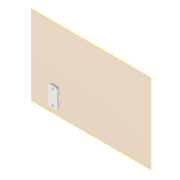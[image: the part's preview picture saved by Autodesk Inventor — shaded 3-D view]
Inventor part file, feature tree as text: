
AUTODESK INVENTOR PART (.ipt)
format: ipt  version: 2022 (Build 260153000, 153)  size: 105,472 bytes
history: native  units: mm
features: reference x6, other x4, extrude x2, sketch x2, plane x1, fillet x1
ambient origin geometry x8: Origin, YZ Plane, XZ Plane, XY Plane, X Axis, Y Axis, Z Axis, Center Point
bodies: Volumenkörper1 (feature_tree)
feature tree (16):
  plane  "Arbeitsebene1"
  extrude  "Extrusion1"  Depth=3.0mm
  fillet  "Rundung1"  Radius=3.0mm
  extrude  "Extrusion2"  Depth=2.0mm
  sketch  "Skizze1"  dims[d0=10.0mm d1=3.0mm d2=3.0mm]
  reference  "Referenz1"
  reference  "Referenz2"
  reference  "Referenz3"
  reference  "Referenz4"
  sketch  "Skizze2"  dims[d3=3.0mm d4=0.0mm d5=2.0mm d6=9.0mm d7=0.0mm d8=0.0mm]
  reference  "Referenz5"
  reference  "Referenz6"
  other  "<userpath>\Documents\GitHub\Guinardia\INVENTOR\Assembly_Guinardia_V1.iam"
  other  "Assembly_Guinardia_V1.iam"
  other  "10_Wellplate_base_v1:1"
  other  "00_CCTV_lens_M12_25mm_5mp:2"
